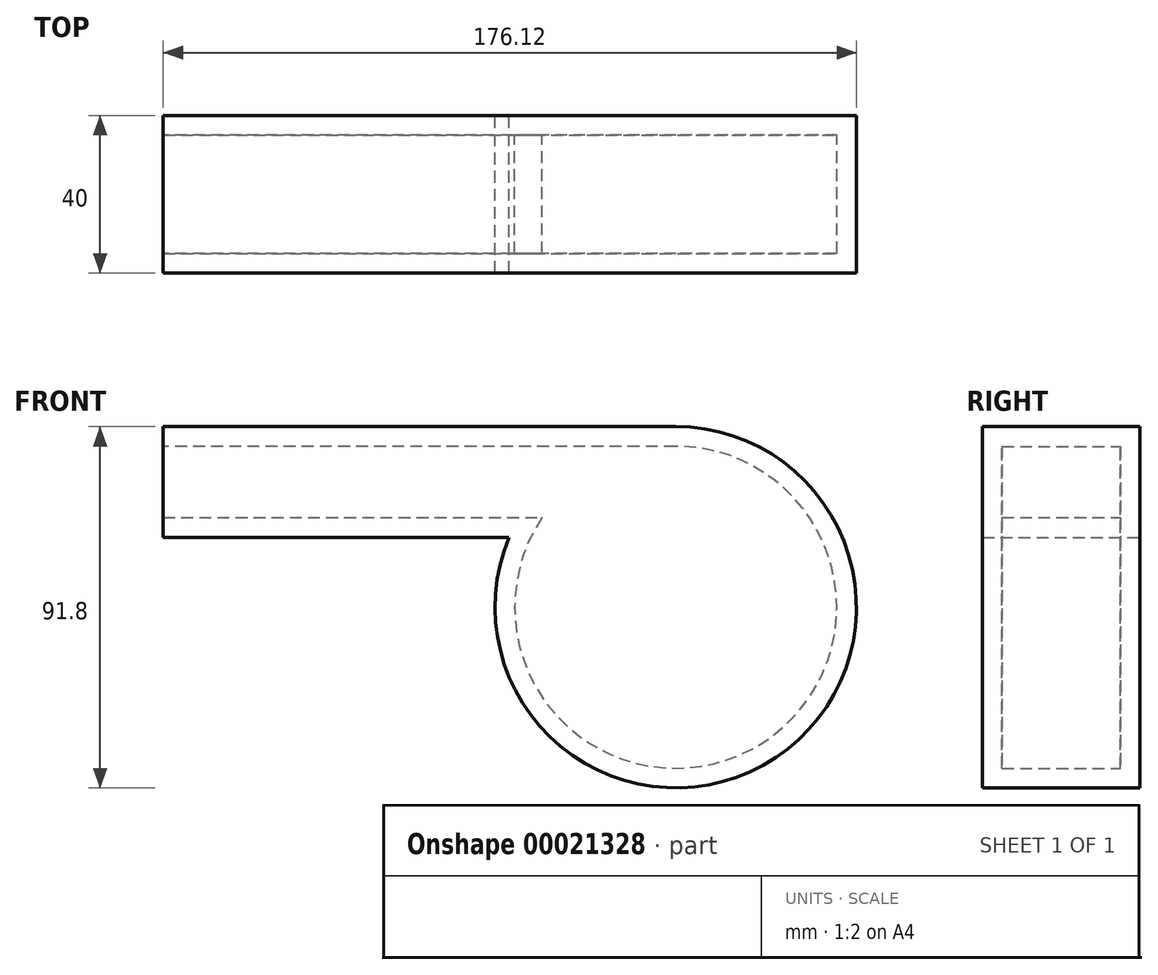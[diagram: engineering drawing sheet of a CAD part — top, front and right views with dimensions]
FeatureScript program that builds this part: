
annotation { "Feature Type Name" : "Feature", "Feature Type Description" : "" }
export const myFeature = defineFeature(function(context is Context, id is Id, definition is map)
    precondition{}
    {
        {
            var Q0;
            Q0=qCreatedBy(makeId("Front.planeOp"),FACE);
            var sketch = newSketch(context, id + "F0", { "sketchPlane" : qUnion([Q0])});
            skArc(sketch, "E0", {"start": v(-42.33, 17.74) * mm, "mid": v(25.42, -38.22) * mm, "end": v(0, 45.9) * mm});
            skLineSegment(sketch, "E1", {"start": v(0, 45.9) * mm, "end": v(-130.22, 45.9) * mm});
            skLineSegment(sketch, "E2", {"start": v(-130.22, 45.9) * mm, "end": v(-130.22, 17.74) * mm});
            skLineSegment(sketch, "E3", {"start": v(-130.22, 17.74) * mm, "end": v(-42.33, 17.74) * mm});
            skSolve(sketch);
        }
        {
            var Q0;
            Q0=makeQuery(id+"F0.imprint","IMPRINT",FACE,{"disambiguationData":[TD([[makeQuery(id+"F0.imprint","IMPRINT",EDGE,{"derivedFrom":sQuery(id+"F0.wireOp",EDGE,"E0")}),1.0]])]});
            extrude(context, id + "F1", {"entities" : qUnion([Q0]), "depth" : 40 * mm});
        }
        {
            var Q0;
            Q0=makeQuery(id+"F1.opExtrude","SWEPT_FACE",FACE,{"disambiguationData":[OSD([sQuery(id+"F0.wireOp",EDGE,"E2")])]});
            shell(context, id + "F2", {"entities" : qUnion([Q0]), "thickness" : 5 * mm});
        }
    });
